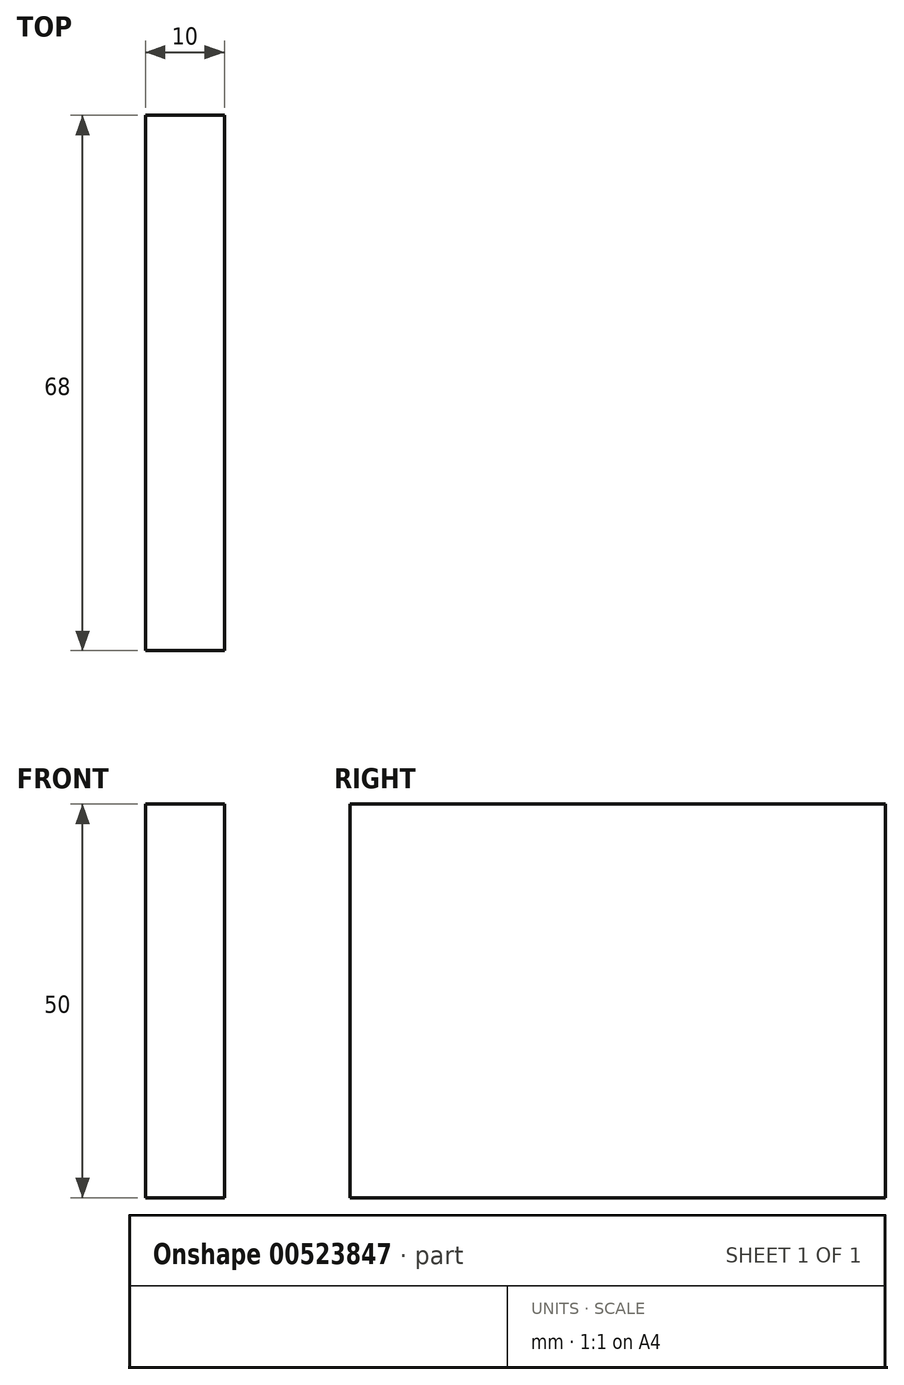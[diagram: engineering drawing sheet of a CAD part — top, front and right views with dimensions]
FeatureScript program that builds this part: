
annotation { "Feature Type Name" : "Feature", "Feature Type Description" : "" }
export const myFeature = defineFeature(function(context is Context, id is Id, definition is map)
    precondition{}
    {
        {
            var Q0;
            Q0=qCreatedBy(makeId("Right.planeOp"),FACE);
            var sketch = newSketch(context, id + "F0", { "sketchPlane" : qUnion([Q0])});
            skLineSegment(sketch, "E0.bottom", {"start": v(-34, 25) * mm, "end": v(34, 25) * mm});
            skLineSegment(sketch, "E0.top", {"start": v(-34, -25) * mm, "end": v(34, -25) * mm});
            skLineSegment(sketch, "E0.left", {"start": v(-34, 25) * mm, "end": v(-34, -25) * mm});
            skLineSegment(sketch, "E0.right", {"start": v(34, 25) * mm, "end": v(34, -25) * mm});
            skPoint(sketch, "E0.middle", {"position": v(0, 0) * mm});
            skSolve(sketch);
        }
        {
            var Q0;
            Q0=makeQuery(id+"F0.imprint","IMPRINT",FACE,{"disambiguationData":[TD([[makeQuery(id+"F0.imprint","IMPRINT",EDGE,{"derivedFrom":sQuery(id+"F0.wireOp",EDGE,"E0.bottom")}),-1.0]])]});
            extrude(context, id + "F1", {"entities" : qUnion([Q0]), "endBound" : BoundingType.SYMMETRIC, "depth" : 10 * mm, "offsetDistance" : 25 * mm});
        }
    });
